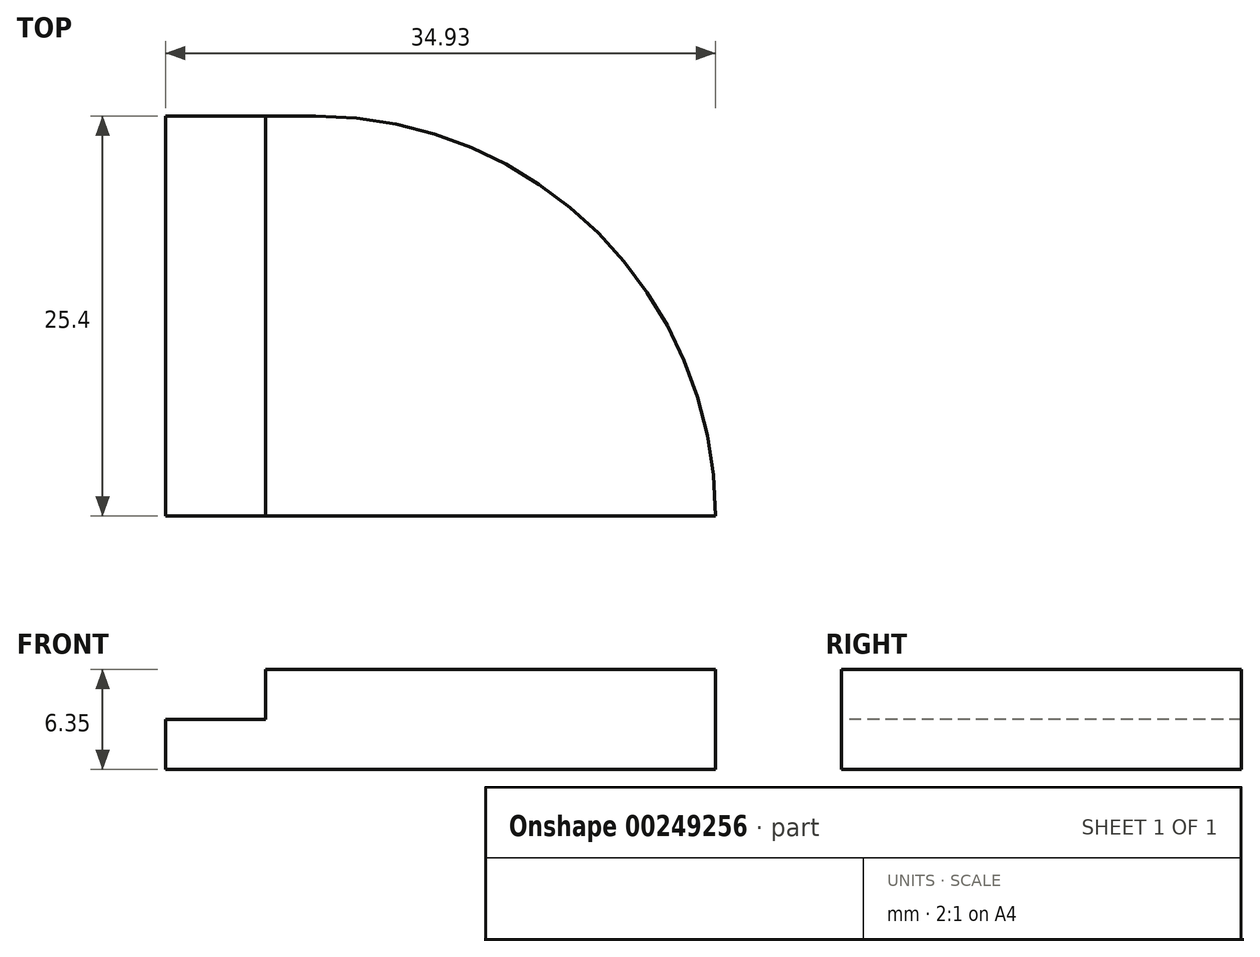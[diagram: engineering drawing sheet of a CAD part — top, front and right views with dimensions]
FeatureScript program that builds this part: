
annotation { "Feature Type Name" : "Feature", "Feature Type Description" : "" }
export const myFeature = defineFeature(function(context is Context, id is Id, definition is map)
    precondition{}
    {
        {
            var Q0;
            Q0=qCreatedBy(makeId("Top.planeOp"),FACE);
            var sketch = newSketch(context, id + "F0", { "sketchPlane" : qUnion([Q0])});
            skLineSegment(sketch, "E0", {"start": v(0, 0) * mm, "end": v(63.5, 0) * mm});
            skPoint(sketch, "E1", {"position": v(25.4, 0) * mm});
            skPoint(sketch, "E2", {"position": v(38.1, 0) * mm});
            skArc(sketch, "E3", {"start": v(0, 0) * mm, "mid": v(7.44, 17.96) * mm, "end": v(25.4, 25.4) * mm});
            skArc(sketch, "E4", {"start": v(63.5, 0) * mm, "mid": v(56.06, 17.96) * mm, "end": v(38.1, 25.4) * mm});
            skLineSegment(sketch, "E5", {"start": v(25.4, 25.4) * mm, "end": v(38.1, 25.4) * mm});
            skPoint(sketch, "E6", {"position": v(28.57, 0) * mm});
            skPoint(sketch, "E7", {"position": v(34.92, 0) * mm});
            skPoint(sketch, "E8", {"position": v(28.57, 25.4) * mm});
            skPoint(sketch, "E9", {"position": v(34.92, 25.4) * mm});
            skLineSegment(sketch, "E10", {"start": v(28.57, 25.4) * mm, "end": v(28.57, 0) * mm});
            skLineSegment(sketch, "E11", {"start": v(34.92, 25.4) * mm, "end": v(34.92, 0) * mm});
            skSolve(sketch);
        }
        {
            var Q0;
            {var subQ0=sQuery(id+"F0.wireOp",EDGE,"E4");Q0=makeQuery(id+"F0.imprint","IMPRINT",FACE,{"disambiguationData":[TD([[makeQuery(id+"F0.imprint","IMPRINT",EDGE,{"derivedFrom":subQ0}),1.0]])]});}
            var Q1;
            {var subQ0=sQuery(id+"F0.wireOp",EDGE,"E3");Q1=makeQuery(id+"F0.imprint","IMPRINT",FACE,{"disambiguationData":[TD([[makeQuery(id+"F0.imprint","IMPRINT",EDGE,{"derivedFrom":subQ0}),-1.0]])]});}
            var Q2;
            {var subQ0=sQuery(id+"F0.wireOp",EDGE,"E10");Q2=makeQuery(id+"F0.imprint","IMPRINT",FACE,{"disambiguationData":[TD([[makeQuery(id+"F0.imprint","IMPRINT",EDGE,{"derivedFrom":subQ0}),1.0]])]});}
            extrude(context, id + "F1", {"entities" : qUnion([Q0, Q1, Q2]), "depth" : 6.35 * mm});
        }
        {
            var Q0;
            Q0=makeQuery(id+"F1.opExtrude","CAP_FACE",FACE,{"disambiguationData":[OSD([sQuery(id+"F0.wireOp",EDGE,"E0"),sQuery(id+"F0.wireOp",EDGE,"E3"),sQuery(id+"F0.wireOp",EDGE,"E4"),sQuery(id+"F0.wireOp",EDGE,"E5")])],"isStart":false});
            var sketch = newSketch(context, id + "F2", { "sketchPlane" : qUnion([Q0])});
            skLineSegment(sketch, "E12", {"start": v(28.58, 0) * mm, "end": v(34.92, 0) * mm});
            skLineSegment(sketch, "E13", {"start": v(34.92, 0) * mm, "end": v(34.92, 25.4) * mm});
            skLineSegment(sketch, "E14", {"start": v(28.57, 0) * mm, "end": v(28.57, 25.4) * mm});
            skLineSegment(sketch, "E15", {"start": v(28.57, 25.4) * mm, "end": v(34.92, 25.4) * mm});
            skSolve(sketch);
        }
        {
            var Q0;
            Q0=makeQuery(id+"F2.imprint","IMPRINT",FACE,{"disambiguationData":[TD([[makeQuery(id+"F2.imprint","IMPRINT",EDGE,{"derivedFrom":sQuery(id+"F2.wireOp",EDGE,"E12")}),1.0]])]});
            extrude(context, id + "F3", {"entities" : qUnion([Q0]), "operationType" : NewBodyOperationType.REMOVE, "oppositeDirection" : true, "depth" : 3.17 * mm});
        }
    });
